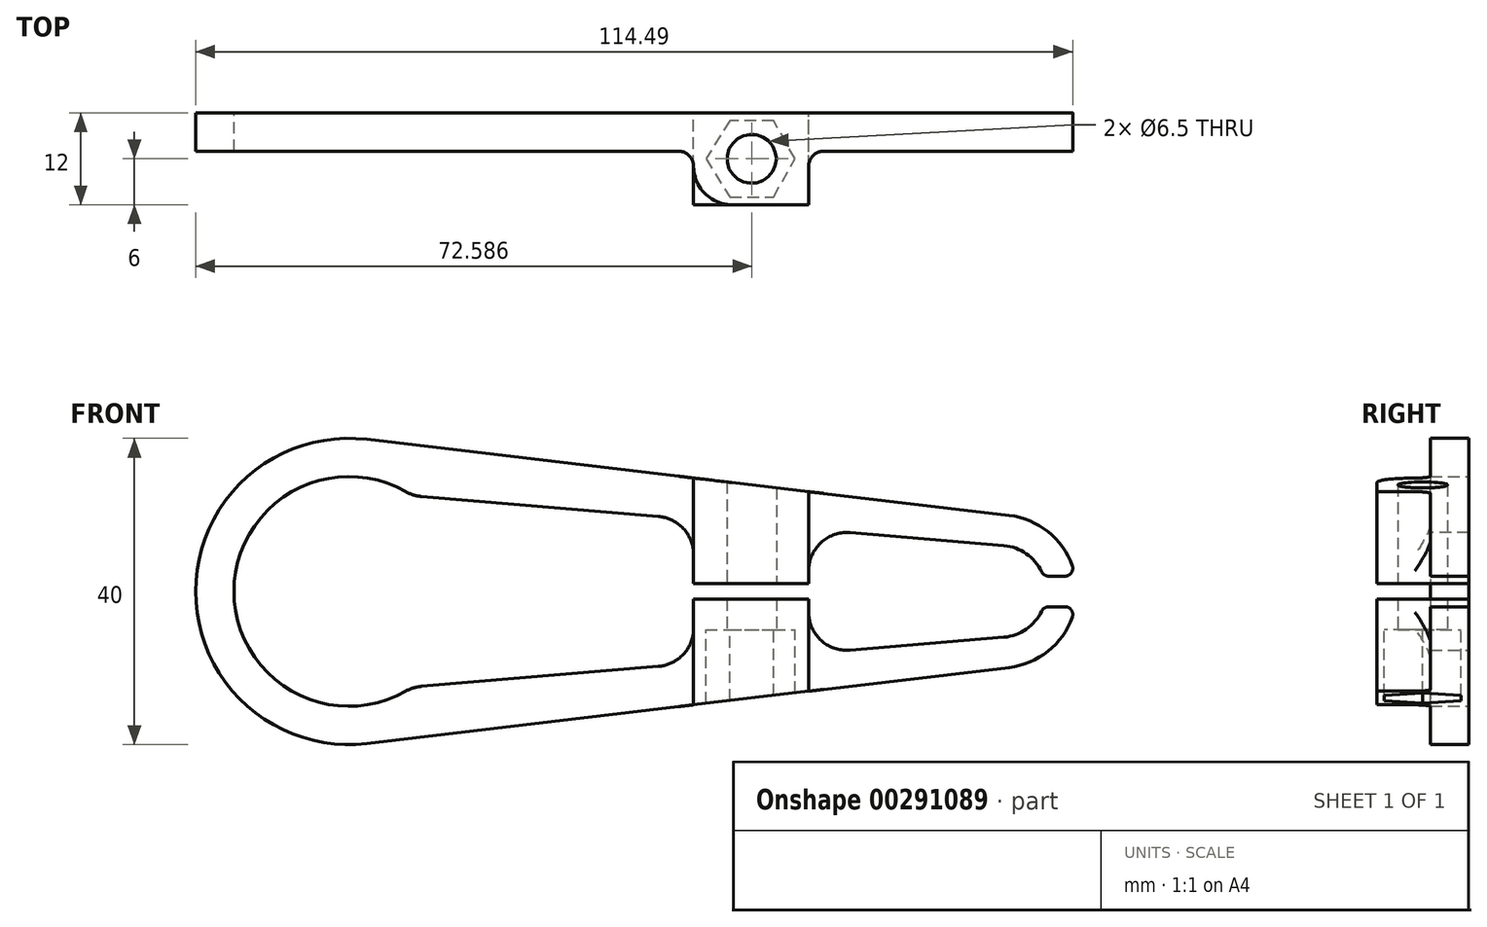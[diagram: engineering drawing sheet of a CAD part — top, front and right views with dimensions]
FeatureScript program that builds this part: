
annotation { "Feature Type Name" : "Feature", "Feature Type Description" : "" }
export const myFeature = defineFeature(function(context is Context, id is Id, definition is map)
    precondition{}
    {
        {
            var Q0;
            Q0=qCreatedBy(makeId("Front.planeOp"),FACE);
            var sketch = newSketch(context, id + "F0", { "sketchPlane" : qUnion([Q0])});
            skArc(sketch, "E0", {"start": v(90.66, 2) * mm, "mid": v(88.67, 4.75) * mm, "end": v(85.5, 5.98) * mm});
            skArc(sketch, "E1", {"start": v(86.18, -9.93) * mm, "mid": v(91.77, -7.36) * mm, "end": v(94.8, -2) * mm});
            skLineSegment(sketch, "E2", {"start": v(2.35, 19.86) * mm, "end": v(2.35, 19.86) * mm});
            skLineSegment(sketch, "E3", {"start": v(2.35, -19.86) * mm, "end": v(2.35, -19.86) * mm});
            skLineSegment(sketch, "E4", {"start": v(8.3, 12.5) * mm, "end": v(45, 9.4) * mm});
            skLineSegment(sketch, "E5", {"start": v(8.3, -12.5) * mm, "end": v(45, -9.4) * mm});
            skLineSegment(sketch, "E6", {"start": v(2.35, 19.86) * mm, "end": v(86.18, 9.93) * mm});
            skLineSegment(sketch, "E7", {"start": v(2.35, -19.86) * mm, "end": v(86.18, -9.93) * mm});
            skArc(sketch, "E8", {"start": v(2.35, 19.86) * mm, "mid": v(-20, 0) * mm, "end": v(2.35, -19.86) * mm});
            skLineSegment(sketch, "E9", {"start": v(94.8, 2) * mm, "end": v(90.66, 2) * mm});
            skLineSegment(sketch, "E10", {"start": v(94.8, -2) * mm, "end": v(90.66, -2) * mm});
            skArc(sketch, "E11.trimOffspring", {"start": v(94.8, 2) * mm, "mid": v(91.77, 7.36) * mm, "end": v(86.18, 9.93) * mm});
            skArc(sketch, "E12.trimOffspring", {"start": v(85.5, -5.98) * mm, "mid": v(88.67, -4.75) * mm, "end": v(90.66, -2) * mm});
            skArc(sketch, "E13", {"start": v(8.3, 12.5) * mm, "mid": v(-15, 0) * mm, "end": v(8.3, -12.5) * mm});
            skPoint(sketch, "E14.orphan", {"position": v(-12.7, 14.27) * mm});
            skPoint(sketch, "E15.orphan", {"position": v(-12.7, -14.27) * mm});
            skLineSegment(sketch, "E16", {"start": v(45, 9.4) * mm, "end": v(45, 1) * mm});
            skLineSegment(sketch, "E17", {"start": v(45, 1) * mm, "end": v(60, 1) * mm});
            skLineSegment(sketch, "E18", {"start": v(60, 1) * mm, "end": v(60, 8.13) * mm});
            skLineSegment(sketch, "E19.trimOffspring", {"start": v(60, 8.13) * mm, "end": v(85.5, 5.98) * mm});
            skLineSegment(sketch, "E20", {"start": v(45, -9.4) * mm, "end": v(45, -1) * mm});
            skLineSegment(sketch, "E21", {"start": v(60, -8.13) * mm, "end": v(60, -1) * mm});
            skLineSegment(sketch, "E22", {"start": v(60, -1) * mm, "end": v(45, -1) * mm});
            skLineSegment(sketch, "E23.trimOffspring", {"start": v(60, -8.13) * mm, "end": v(85.5, -5.98) * mm});
            skSolve(sketch);
        }
        {
            var Q0;
            Q0=makeQuery(id+"F0.imprint","IMPRINT",FACE,{"disambiguationData":[TD([[makeQuery(id+"F0.imprint","IMPRINT",EDGE,{"derivedFrom":sQuery(id+"F0.wireOp",EDGE,"E0")}),-1.0]])]});
            extrude(context, id + "F1", {"entities" : qUnion([Q0]), "depth" : 12 * mm});
        }
        {
            var Q0;
            Q0=makeQuery(id+"F1.opExtrude","CAP_FACE",FACE,{"disambiguationData":[OSD([sQuery(id+"F0.wireOp",EDGE,"E0"),sQuery(id+"F0.wireOp",EDGE,"E1"),sQuery(id+"F0.wireOp",EDGE,"E4"),sQuery(id+"F0.wireOp",EDGE,"E5"),sQuery(id+"F0.wireOp",EDGE,"E6"),sQuery(id+"F0.wireOp",EDGE,"E7"),sQuery(id+"F0.wireOp",EDGE,"E8"),sQuery(id+"F0.wireOp",EDGE,"E9"),sQuery(id+"F0.wireOp",EDGE,"E10"),sQuery(id+"F0.wireOp",EDGE,"E11.trimOffspring"),sQuery(id+"F0.wireOp",EDGE,"E12.trimOffspring"),sQuery(id+"F0.wireOp",EDGE,"E13"),sQuery(id+"F0.wireOp",EDGE,"E16"),sQuery(id+"F0.wireOp",EDGE,"E17"),sQuery(id+"F0.wireOp",EDGE,"E18"),sQuery(id+"F0.wireOp",EDGE,"E19.trimOffspring"),sQuery(id+"F0.wireOp",EDGE,"E20"),sQuery(id+"F0.wireOp",EDGE,"E21"),sQuery(id+"F0.wireOp",EDGE,"E22"),sQuery(id+"F0.wireOp",EDGE,"E23.trimOffspring")])],"isStart":false});
            var sketch = newSketch(context, id + "F2", { "sketchPlane" : qUnion([Q0])});
            skLineSegment(sketch, "E24.0", {"start": v(45, 14.8) * mm, "end": v(45, 1) * mm});
            skLineSegment(sketch, "E25.0", {"start": v(2.35, 19.86) * mm, "end": v(45, 14.8) * mm});
            skArc(sketch, "E26.0", {"start": v(2.35, 19.86) * mm, "mid": v(-20, 0) * mm, "end": v(2.35, -19.86) * mm});
            skLineSegment(sketch, "E27.0", {"start": v(2.35, -19.86) * mm, "end": v(45, -14.8) * mm});
            skLineSegment(sketch, "E28.0", {"start": v(45, -14.8) * mm, "end": v(45, -1) * mm});
            skLineSegment(sketch, "E29.0", {"start": v(8.3, -12.5) * mm, "end": v(45, -9.4) * mm});
            skArc(sketch, "E30.0", {"start": v(8.3, 12.5) * mm, "mid": v(-15, 0) * mm, "end": v(8.3, -12.5) * mm});
            skLineSegment(sketch, "E31.0", {"start": v(8.3, 12.5) * mm, "end": v(45, 9.4) * mm});
            skPoint(sketch, "E32.orphan", {"position": v(86.18, 9.93) * mm});
            skPoint(sketch, "E33.orphan", {"position": v(86.18, -9.93) * mm});
            skSolve(sketch);
        }
        {
            var Q0;
            {var subQ1=sQuery(id+"F2.wireOp",EDGE,"E25.0");Q0=makeQuery(id+"F2.imprint","IMPRINT",FACE,{"disambiguationData":[TD([[makeQuery(id+"F2.imprint","IMPRINT",EDGE,{"derivedFrom":subQ1}),-1.0]])]});}
            extrude(context, id + "F3", {"entities" : qUnion([Q0]), "operationType" : NewBodyOperationType.REMOVE, "oppositeDirection" : true, "depth" : 7 * mm});
        }
        {
            var Q0;
            {var subQ0=sQuery(id+"F0.wireOp",EDGE,"E10");var subQ1=sQuery(id+"F0.wireOp",EDGE,"E23.trimOffspring");var subQ2=sQuery(id+"F0.wireOp",EDGE,"E12.trimOffspring");var subQ3=sQuery(id+"F0.wireOp",EDGE,"E7");var subQ4=sQuery(id+"F0.wireOp",EDGE,"E20");var subQ5=sQuery(id+"F0.wireOp",EDGE,"E1");var subQ6=sQuery(id+"F0.wireOp",EDGE,"E21");var subQ7=sQuery(id+"F0.wireOp",EDGE,"E22");Q0=makeQuery(id+"F3.boolean.opBoolean","SPLIT",FACE,{"disambiguationData":[TD([makeQuery(id+"F1.opExtrude","SWEPT_FACE",FACE,{"disambiguationData":[OSD([subQ5])]})])],"derivedFrom":makeQuery(id+"F1.opExtrude","CAP_FACE",FACE,{"disambiguationData":[OSD([sQuery(id+"F0.wireOp",EDGE,"E0"),subQ5,sQuery(id+"F0.wireOp",EDGE,"E4"),sQuery(id+"F0.wireOp",EDGE,"E5"),sQuery(id+"F0.wireOp",EDGE,"E6"),subQ3,sQuery(id+"F0.wireOp",EDGE,"E8"),sQuery(id+"F0.wireOp",EDGE,"E9"),subQ0,sQuery(id+"F0.wireOp",EDGE,"E11.trimOffspring"),subQ2,sQuery(id+"F0.wireOp",EDGE,"E13"),sQuery(id+"F0.wireOp",EDGE,"E16"),sQuery(id+"F0.wireOp",EDGE,"E17"),sQuery(id+"F0.wireOp",EDGE,"E18"),sQuery(id+"F0.wireOp",EDGE,"E19.trimOffspring"),subQ4,subQ6,subQ7,subQ1])],"isStart":false})});}
            var sketch = newSketch(context, id + "F4", { "sketchPlane" : qUnion([Q0])});
            skLineSegment(sketch, "E34.0", {"start": v(60, 8.13) * mm, "end": v(85.5, 5.98) * mm});
            skLineSegment(sketch, "E35.0", {"start": v(60, 8.13) * mm, "end": v(60, 13.03) * mm});
            skLineSegment(sketch, "E36.0", {"start": v(60, -13.03) * mm, "end": v(60, -8.13) * mm});
            skLineSegment(sketch, "E37.0", {"start": v(60, -8.13) * mm, "end": v(85.5, -5.98) * mm});
            skArc(sketch, "E38.0", {"start": v(85.5, -5.98) * mm, "mid": v(88.67, -4.75) * mm, "end": v(90.66, -2) * mm});
            skArc(sketch, "E39.0", {"start": v(90.66, 2) * mm, "mid": v(88.67, 4.75) * mm, "end": v(85.5, 5.98) * mm});
            skLineSegment(sketch, "E40.0", {"start": v(94.8, 2) * mm, "end": v(90.66, 2) * mm});
            skLineSegment(sketch, "E41.0", {"start": v(94.8, -2) * mm, "end": v(90.66, -2) * mm});
            skArc(sketch, "E42.0", {"start": v(94.8, 2) * mm, "mid": v(91.77, 7.36) * mm, "end": v(86.18, 9.93) * mm});
            skLineSegment(sketch, "E43.0", {"start": v(60, 13.03) * mm, "end": v(86.18, 9.93) * mm});
            skArc(sketch, "E44.0", {"start": v(86.18, -9.93) * mm, "mid": v(91.77, -7.36) * mm, "end": v(94.8, -2) * mm});
            skLineSegment(sketch, "E45.0", {"start": v(60, -13.03) * mm, "end": v(86.18, -9.93) * mm});
            skPoint(sketch, "E46.orphan", {"position": v(45, 14.8) * mm});
            skPoint(sketch, "E47.orphan", {"position": v(60, 1) * mm});
            skPoint(sketch, "E48.orphan", {"position": v(60, -1) * mm});
            skPoint(sketch, "E49.orphan", {"position": v(45, -14.8) * mm});
            skSolve(sketch);
        }
        {
            var Q0;
            Q0 = qSketchRegion(id + "F4", true);
            extrude(context, id + "F5", {"entities" : qUnion([Q0]), "operationType" : NewBodyOperationType.REMOVE, "oppositeDirection" : true, "depth" : 7 * mm});
        }
        {
            var Q0;
            Q0=makeQuery(id+"F5.boolean.opBoolean","COPY",EDGE,{"derivedFrom":makeQuery(id+"F5.opExtrude","CAP_EDGE",EDGE,{"disambiguationData":[OSD([sQuery(id+"F4.wireOp",EDGE,"E35.0")])],"isStart":false})});
            var Q1;
            Q1=makeQuery(id+"F5.boolean.opBoolean","COPY",EDGE,{"derivedFrom":makeQuery(id+"F5.opExtrude","CAP_EDGE",EDGE,{"disambiguationData":[OSD([sQuery(id+"F4.wireOp",EDGE,"E36.0")])],"isStart":false})});
            var Q2;
            Q2=makeQuery(id+"F3.boolean.opBoolean","COPY",EDGE,{"derivedFrom":makeQuery(id+"F3.opExtrude","CAP_EDGE",EDGE,{"disambiguationData":[OSD([sQuery(id+"F2.wireOp",EDGE,"E24.0")])],"isStart":false})});
            var Q3;
            Q3=makeQuery(id+"F3.boolean.opBoolean","COPY",EDGE,{"derivedFrom":makeQuery(id+"F3.opExtrude","CAP_EDGE",EDGE,{"disambiguationData":[OSD([sQuery(id+"F2.wireOp",EDGE,"E28.0")])],"isStart":false})});
            fillet(context, id + "F6", {"entities" : qUnion([Q0, Q1, Q2, Q3]), "radius" : 2 * mm, "tangentPropagation" : true, "allowEdgeOverflow" : false});
        }
        {
            var Q0;
            Q0=makeQuery(id+"F5.boolean.opBoolean","MERGE",EDGE,{"derivedFrom":[makeQuery(id+"F1.opExtrude","CAP_EDGE",EDGE,{"disambiguationData":[OSD([sQuery(id+"F0.wireOp",EDGE,"E18")])],"isStart":false}),makeQuery(id+"F5.opExtrude","CAP_EDGE",EDGE,{"disambiguationData":[OSD([sQuery(id+"F4.wireOp",EDGE,"E35.0")])],"isStart":true})]});
            var Q1;
            Q1=makeQuery(id+"F5.boolean.opBoolean","MERGE",EDGE,{"derivedFrom":[makeQuery(id+"F1.opExtrude","CAP_EDGE",EDGE,{"disambiguationData":[OSD([sQuery(id+"F0.wireOp",EDGE,"E21")])],"isStart":false}),makeQuery(id+"F5.opExtrude","CAP_EDGE",EDGE,{"disambiguationData":[OSD([sQuery(id+"F4.wireOp",EDGE,"E36.0")])],"isStart":true})]});
            var Q2;
            Q2=makeQuery(id+"F3.boolean.opBoolean","MERGE",EDGE,{"derivedFrom":[makeQuery(id+"F1.opExtrude","CAP_EDGE",EDGE,{"disambiguationData":[OSD([sQuery(id+"F0.wireOp",EDGE,"E16")])],"isStart":false}),makeQuery(id+"F3.opExtrude","CAP_EDGE",EDGE,{"disambiguationData":[OSD([sQuery(id+"F2.wireOp",EDGE,"E24.0")])],"isStart":true})]});
            var Q3;
            Q3=makeQuery(id+"F3.boolean.opBoolean","MERGE",EDGE,{"derivedFrom":[makeQuery(id+"F1.opExtrude","CAP_EDGE",EDGE,{"disambiguationData":[OSD([sQuery(id+"F0.wireOp",EDGE,"E20")])],"isStart":false}),makeQuery(id+"F3.opExtrude","CAP_EDGE",EDGE,{"disambiguationData":[OSD([sQuery(id+"F2.wireOp",EDGE,"E28.0")])],"isStart":true})]});
            fillet(context, id + "F7", {"entities" : qUnion([Q0, Q1, Q2, Q3]), "radius" : 5 * mm, "tangentPropagation" : true, "allowEdgeOverflow" : false});
        }
        {
            var Q0;
            Q0=qCreatedBy(makeId("Top.planeOp"),FACE);
            cPlane(context, id + "F8", {"entities" : qUnion([Q0]), "cplaneType" : CPlaneType.OFFSET, "offset" : 5 * mm, "oppositeDirection" : true, "width" : 150 * mm, "height" : 150 * mm});
        }
        {
            var Q0;
            Q0=qCreatedBy(id+"F8.planeOp",FACE);
            var sketch = newSketch(context, id + "F9", { "sketchPlane" : qUnion([Q0])});
            skCircle(sketch, "E50", {"center": v(52.5, -6) * mm, "radius": 5 * mm, "construction": true});
            skLineSegment(sketch, "E51", {"start": v(49.73, -11) * mm, "end": v(55.44, -11) * mm});
            skLineSegment(sketch, "E52", {"start": v(55.44, -11) * mm, "end": v(58.22, -6) * mm});
            skLineSegment(sketch, "E53", {"start": v(58.22, -6) * mm, "end": v(55.44, -1) * mm});
            skLineSegment(sketch, "E54", {"start": v(55.44, -1) * mm, "end": v(49.73, -1) * mm});
            skLineSegment(sketch, "E55", {"start": v(49.73, -1) * mm, "end": v(46.6, -6) * mm});
            skLineSegment(sketch, "E56", {"start": v(46.6, -6) * mm, "end": v(49.73, -11) * mm});
            skSolve(sketch);
        }
        {
            var Q0;
            Q0 = qSketchRegion(id + "F9", true);
            extrude(context, id + "F10", {"entities" : qUnion([Q0]), "operationType" : NewBodyOperationType.REMOVE, "endBound" : BoundingType.THROUGH_ALL, "oppositeDirection" : true, "depth" : 25 * mm});
        }
        {
            var Q0;
            Q0=makeQuery(id+"F10.boolean.opBoolean","COPY",FACE,{"derivedFrom":makeQuery(id+"F10.opExtrude","CAP_FACE",FACE,{"disambiguationData":[OSD([sQuery(id+"F9.wireOp",EDGE,"E51"),sQuery(id+"F9.wireOp",EDGE,"E52"),sQuery(id+"F9.wireOp",EDGE,"E53"),sQuery(id+"F9.wireOp",EDGE,"E54"),sQuery(id+"F9.wireOp",EDGE,"E55"),sQuery(id+"F9.wireOp",EDGE,"E56")])],"isStart":true})});
            var sketch = newSketch(context, id + "F11", { "sketchPlane" : qUnion([Q0])});
            skLineSegment(sketch, "E57", {"start": v(49.73, 11) * mm, "end": v(52.59, 6) * mm, "construction": true});
            skLineSegment(sketch, "E58", {"start": v(55.44, 11) * mm, "end": v(52.59, 6) * mm, "construction": true});
            skCircle(sketch, "E59", {"center": v(52.59, 6) * mm, "radius": 3.25 * mm});
            skSolve(sketch);
        }
        {
            var Q0;
            Q0 = qSketchRegion(id + "F11", true);
            extrude(context, id + "F12", {"entities" : qUnion([Q0]), "operationType" : NewBodyOperationType.REMOVE, "endBound" : BoundingType.THROUGH_ALL, "oppositeDirection" : true, "depth" : 25 * mm});
        }
        {
            var Q0;
            Q0=makeQuery(id+"F1.opExtrude","SWEPT_EDGE",EDGE,{"disambiguationData":[OSD([sQuery(id+"F0.wireOp",EDGE,"E4"),sQuery(id+"F0.wireOp",EDGE,"E13")])]});
            var Q1;
            Q1=makeQuery(id+"F1.opExtrude","SWEPT_EDGE",EDGE,{"disambiguationData":[OSD([sQuery(id+"F0.wireOp",EDGE,"E5"),sQuery(id+"F0.wireOp",EDGE,"E13")])]});
            var Q2;
            Q2=makeQuery(id+"F1.opExtrude","SWEPT_EDGE",EDGE,{"disambiguationData":[OSD([sQuery(id+"F0.wireOp",EDGE,"E4"),sQuery(id+"F0.wireOp",EDGE,"E16")])]});
            var Q3;
            Q3=makeQuery(id+"F1.opExtrude","SWEPT_EDGE",EDGE,{"disambiguationData":[OSD([sQuery(id+"F0.wireOp",EDGE,"E5"),sQuery(id+"F0.wireOp",EDGE,"E20")])]});
            var Q4;
            Q4=makeQuery(id+"F1.opExtrude","SWEPT_EDGE",EDGE,{"disambiguationData":[OSD([sQuery(id+"F0.wireOp",EDGE,"E21"),sQuery(id+"F0.wireOp",EDGE,"E23.trimOffspring")])]});
            var Q5;
            Q5=makeQuery(id+"F1.opExtrude","SWEPT_EDGE",EDGE,{"disambiguationData":[OSD([sQuery(id+"F0.wireOp",EDGE,"E18"),sQuery(id+"F0.wireOp",EDGE,"E19.trimOffspring")])]});
            fillet(context, id + "F13", {"entities" : qUnion([Q0, Q1, Q2, Q3, Q4, Q5]), "radius" : 5 * mm, "tangentPropagation" : true, "allowEdgeOverflow" : false});
        }
        {
            var Q0;
            Q0=makeQuery(id+"F1.opExtrude","SWEPT_EDGE",EDGE,{"disambiguationData":[OSD([sQuery(id+"F0.wireOp",EDGE,"E10"),sQuery(id+"F0.wireOp",EDGE,"E12.trimOffspring")])]});
            var Q1;
            Q1=makeQuery(id+"F1.opExtrude","SWEPT_EDGE",EDGE,{"disambiguationData":[OSD([sQuery(id+"F0.wireOp",EDGE,"E0"),sQuery(id+"F0.wireOp",EDGE,"E9")])]});
            var Q2;
            Q2=makeQuery(id+"F1.opExtrude","SWEPT_EDGE",EDGE,{"disambiguationData":[OSD([sQuery(id+"F0.wireOp",EDGE,"E1"),sQuery(id+"F0.wireOp",EDGE,"E10")])]});
            var Q3;
            Q3=makeQuery(id+"F1.opExtrude","SWEPT_EDGE",EDGE,{"disambiguationData":[OSD([sQuery(id+"F0.wireOp",EDGE,"E9"),sQuery(id+"F0.wireOp",EDGE,"E11.trimOffspring")])]});
            fillet(context, id + "F14", {"entities" : qUnion([Q0, Q1, Q2, Q3]), "radius" : 1 * mm, "tangentPropagation" : true, "allowEdgeOverflow" : false});
        }
    });
